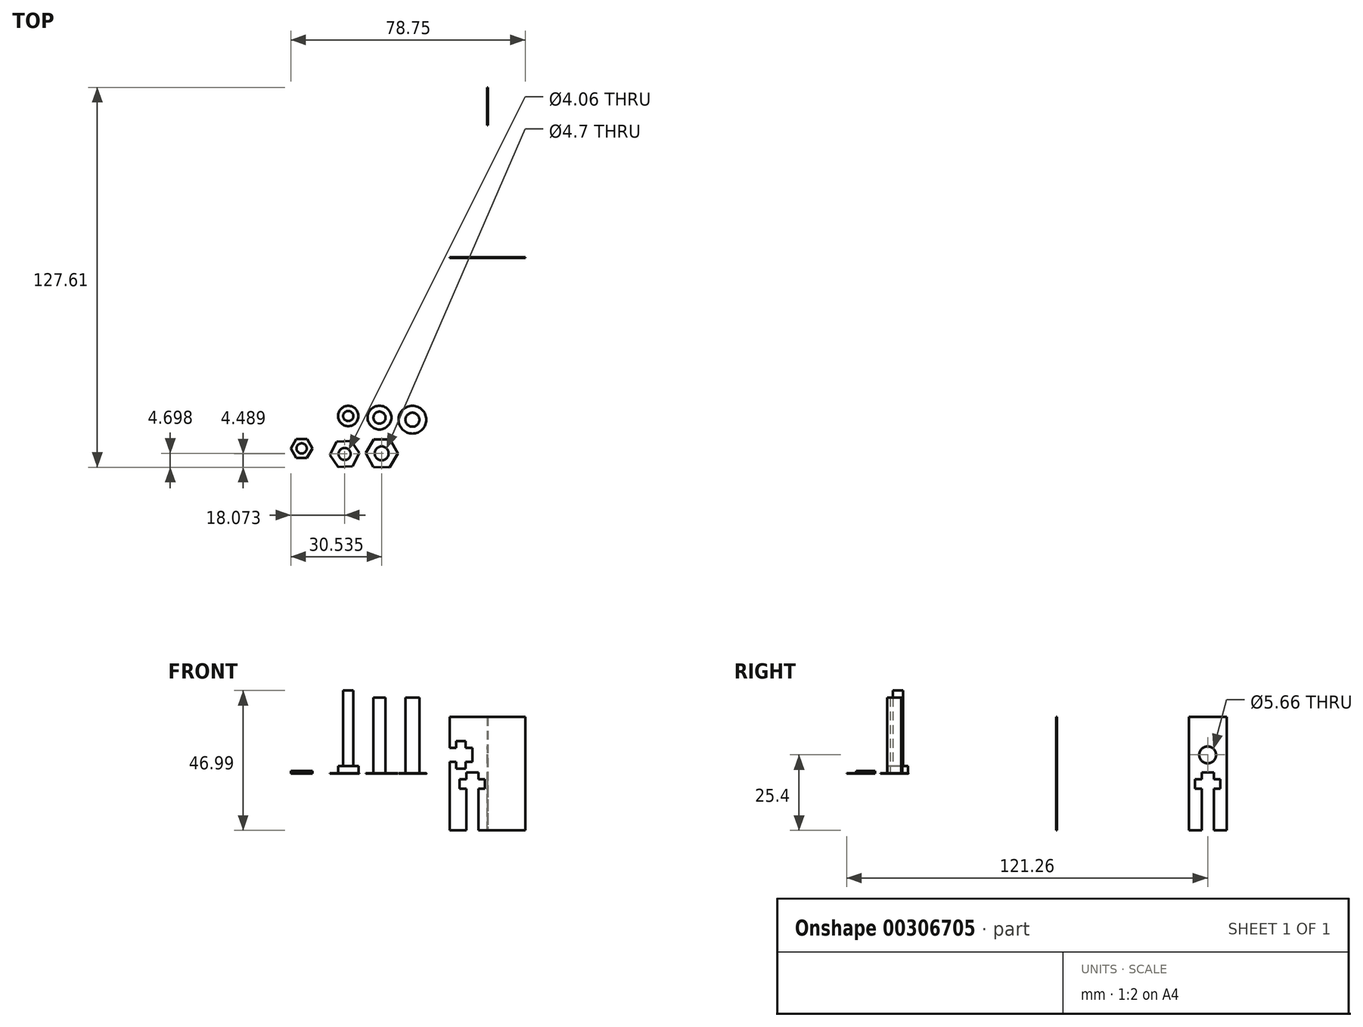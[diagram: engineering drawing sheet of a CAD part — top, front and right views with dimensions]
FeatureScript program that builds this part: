
annotation { "Feature Type Name" : "Feature", "Feature Type Description" : "" }
export const myFeature = defineFeature(function(context is Context, id is Id, definition is map)
    precondition{}
    {
        {
            assignVariable(context, id + "F0", {"name" : "mdfThick", "anyValue" : .235});
        }
        {
            var Q0;
            Q0=qCreatedBy(makeId("Front.planeOp"),FACE);
            var sketch = newSketch(context, id + "F1", { "sketchPlane" : qUnion([Q0])});
            skLineSegment(sketch, "E0.bottom", {"start": v(12.7, 19.05) * mm, "end": v(-12.7, 19.05) * mm});
            skLineSegment(sketch, "E0.top", {"start": v(12.7, -19.05) * mm, "end": v(-12.7, -19.05) * mm});
            skLineSegment(sketch, "E0.left", {"start": v(12.7, 19.05) * mm, "end": v(12.7, -19.05) * mm});
            skLineSegment(sketch, "E0.right", {"start": v(-12.7, 19.05) * mm, "end": v(-12.7, -19.05) * mm});
            skPoint(sketch, "E0.middle", {"position": v(0, 0) * mm});
            skSolve(sketch);
        }
        {
            var Q0;
            Q0 = qSketchRegion(id + "F1", true);
            extrude(context, id + "F2", {"entities" : qUnion([Q0]), "depth" : (getVariable(context, 'mdfThick')) * mm, "symmetric" : true});
        }
        {
            assignVariable(context, id + "F3", {"name" : "h1024", "anyValue" : .125});
        }
        {
            assignVariable(context, id + "F4", {"name" : "h632", "anyValue" : .95});
        }
        {
            assignVariable(context, id + "F5", {"name" : "h836", "anyValue" : .124});
        }
        {
            var Q0;
            Q0=makeQuery(id+"F2.opExtrude","CAP_FACE",FACE,{"disambiguationData":[OSD([sQuery(id+"F1.wireOp",EDGE,"E0.bottom"),sQuery(id+"F1.wireOp",EDGE,"E0.top"),sQuery(id+"F1.wireOp",EDGE,"E0.left"),sQuery(id+"F1.wireOp",EDGE,"E0.right")])],"isStart":false});
            var sketch = newSketch(context, id + "F6", { "sketchPlane" : qUnion([Q0])});
            skLineSegment(sketch, "E1", {"start": v(-12.7, -19.05) * mm, "end": v(-5.08, -19.05) * mm});
            skLineSegment(sketch, "E2", {"start": v(-12.7, -19.05) * mm, "end": v(-12.7, 6.35) * mm});
            skLineSegment(sketch, "E3.bottom", {"start": v(-5.08, 4) * mm, "end": v(-20.32, 4) * mm});
            skLineSegment(sketch, "E3.top", {"start": v(-5.08, 8.7) * mm, "end": v(-20.32, 8.7) * mm});
            skLineSegment(sketch, "E3.left", {"start": v(-5.08, 4) * mm, "end": v(-5.08, 8.7) * mm});
            skLineSegment(sketch, "E3.right", {"start": v(-20.32, 4) * mm, "end": v(-20.32, 8.7) * mm});
            skPoint(sketch, "E3.middle", {"position": v(-12.7, 6.35) * mm});
            skLineSegment(sketch, "E4.bottom", {"start": v(-3.05, 0.38) * mm, "end": v(-7.11, 0.38) * mm});
            skLineSegment(sketch, "E4.top", {"start": v(-3.05, -38.48) * mm, "end": v(-7.11, -38.48) * mm});
            skLineSegment(sketch, "E4.left", {"start": v(-3.05, 0.38) * mm, "end": v(-3.05, -38.48) * mm});
            skLineSegment(sketch, "E4.right", {"start": v(-7.11, 0.38) * mm, "end": v(-7.11, -38.48) * mm});
            skPoint(sketch, "E4.middle", {"position": v(-5.08, -19.05) * mm});
            skLineSegment(sketch, "E5", {"start": v(-5.08, 6.35) * mm, "end": v(-8.9, 6.35) * mm});
            skLineSegment(sketch, "E6.bottom", {"start": v(-7.3, 11.02) * mm, "end": v(-10.48, 11.02) * mm});
            skLineSegment(sketch, "E6.top", {"start": v(-7.3, 1.68) * mm, "end": v(-10.48, 1.68) * mm});
            skLineSegment(sketch, "E6.left", {"start": v(-7.3, 11.02) * mm, "end": v(-7.3, 1.68) * mm});
            skLineSegment(sketch, "E6.right", {"start": v(-10.48, 11.02) * mm, "end": v(-10.48, 1.68) * mm});
            skPoint(sketch, "E6.middle", {"position": v(-8.9, 6.35) * mm});
            skLineSegment(sketch, "E7", {"start": v(-5.08, 0.38) * mm, "end": v(-5.08, -3.43) * mm});
            skLineSegment(sketch, "E8.bottom", {"start": v(-0.83, -1.85) * mm, "end": v(-9.33, -1.85) * mm});
            skLineSegment(sketch, "E8.top", {"start": v(-0.83, -5) * mm, "end": v(-9.33, -5) * mm});
            skLineSegment(sketch, "E8.left", {"start": v(-0.83, -1.85) * mm, "end": v(-0.83, -5) * mm});
            skLineSegment(sketch, "E8.right", {"start": v(-9.33, -1.85) * mm, "end": v(-9.33, -5) * mm});
            skPoint(sketch, "E8.middle", {"position": v(-5.08, -3.43) * mm});
            skSolve(sketch);
        }
        {
            var Q0;
            {var subQ5=makeQuery(id+"F2.opExtrude","CAP_EDGE",EDGE,{"disambiguationData":[OSD([sQuery(id+"F1.wireOp",EDGE,"E0.right")])],"isStart":false});var subQ7=sQuery(id+"F6.wireOp",EDGE,"E2");var subQ9=makeQuery(id+"F6.imprint","INTERSECT",VERTEX,{"derivedFrom":[subQ5,subQ7]});Q0=makeQuery(id+"F6.imprint","IMPRINT",FACE,{"disambiguationData":[TD([[makeQuery(id+"F6.imprint","IMPRINT",EDGE,{"disambiguationData":[TD([[subQ9,-1.0]])],"derivedFrom":subQ7}),1.0]])]});}
            var Q1;
            {var subQ5=sQuery(id+"F6.wireOp",EDGE,"E6.bottom");Q1=makeQuery(id+"F6.imprint","IMPRINT",FACE,{"disambiguationData":[TD([[makeQuery(id+"F6.imprint","IMPRINT",EDGE,{"derivedFrom":subQ5}),1.0]])]});}
            var Q2;
            {var subQ0=sQuery(id+"F6.wireOp",EDGE,"E6.left");var subQ2=sQuery(id+"F6.wireOp",EDGE,"E3.bottom");var subQ3=makeQuery(id+"F6.imprint","INTERSECT",VERTEX,{"derivedFrom":[subQ2,subQ0]});Q2=makeQuery(id+"F6.imprint","IMPRINT",FACE,{"disambiguationData":[TD([[makeQuery(id+"F6.imprint","IMPRINT",EDGE,{"disambiguationData":[TD([[subQ3,-1.0]])],"derivedFrom":subQ2}),-1.0]])]});}
            var Q3;
            {var subQ0=sQuery(id+"F6.wireOp",EDGE,"E3.left");var subQ1=sQuery(id+"F6.wireOp",EDGE,"E3.top");var subQ2=makeQuery(id+"F6.imprint","INTERSECT",VERTEX,{"derivedFrom":[subQ1,subQ0]});Q3=makeQuery(id+"F6.imprint","IMPRINT",FACE,{"disambiguationData":[TD([[makeQuery(id+"F6.imprint","IMPRINT",EDGE,{"disambiguationData":[TD([[subQ2,-1.0]])],"derivedFrom":subQ1}),1.0]])]});}
            var Q4;
            {var subQ0=sQuery(id+"F6.wireOp",EDGE,"E3.left");var subQ1=sQuery(id+"F6.wireOp",EDGE,"E3.bottom");var subQ2=makeQuery(id+"F6.imprint","INTERSECT",VERTEX,{"derivedFrom":[subQ1,subQ0]});Q4=makeQuery(id+"F6.imprint","IMPRINT",FACE,{"disambiguationData":[TD([[makeQuery(id+"F6.imprint","IMPRINT",EDGE,{"disambiguationData":[TD([[subQ2,-1.0]])],"derivedFrom":subQ1}),-1.0]])]});}
            var Q5;
            {var subQ5=sQuery(id+"F6.wireOp",EDGE,"E6.top");Q5=makeQuery(id+"F6.imprint","IMPRINT",FACE,{"disambiguationData":[TD([[makeQuery(id+"F6.imprint","IMPRINT",EDGE,{"derivedFrom":subQ5}),-1.0]])]});}
            var Q6;
            {var subQ0=sQuery(id+"F6.wireOp",EDGE,"E4.left");var subQ1=sQuery(id+"F6.wireOp",EDGE,"E4.bottom");var subQ2=makeQuery(id+"F6.imprint","INTERSECT",VERTEX,{"derivedFrom":[subQ1,subQ0]});Q6=makeQuery(id+"F6.imprint","IMPRINT",FACE,{"disambiguationData":[TD([[makeQuery(id+"F6.imprint","IMPRINT",EDGE,{"disambiguationData":[TD([[subQ2,-1.0]])],"derivedFrom":subQ1}),1.0]])]});}
            var Q7;
            {var subQ0=sQuery(id+"F6.wireOp",EDGE,"E4.right");var subQ1=sQuery(id+"F6.wireOp",EDGE,"E4.bottom");var subQ2=makeQuery(id+"F6.imprint","INTERSECT",VERTEX,{"derivedFrom":[subQ1,subQ0]});Q7=makeQuery(id+"F6.imprint","IMPRINT",FACE,{"disambiguationData":[TD([[makeQuery(id+"F6.imprint","IMPRINT",EDGE,{"disambiguationData":[TD([[subQ2,1.0]])],"derivedFrom":subQ1}),1.0]])]});}
            var Q8;
            {var subQ0=sQuery(id+"F6.wireOp",EDGE,"E8.bottom");var subQ2=sQuery(id+"F6.wireOp",EDGE,"E4.left");var subQ3=makeQuery(id+"F6.imprint","INTERSECT",VERTEX,{"derivedFrom":[subQ2,subQ0]});Q8=makeQuery(id+"F6.imprint","IMPRINT",FACE,{"disambiguationData":[TD([[makeQuery(id+"F6.imprint","IMPRINT",EDGE,{"disambiguationData":[TD([[subQ3,-1.0]])],"derivedFrom":subQ2}),-1.0]])]});}
            var Q9;
            {var subQ5=sQuery(id+"F6.wireOp",EDGE,"E8.right");Q9=makeQuery(id+"F6.imprint","IMPRINT",FACE,{"disambiguationData":[TD([[makeQuery(id+"F6.imprint","IMPRINT",EDGE,{"derivedFrom":subQ5}),1.0]])]});}
            var Q10;
            {var subQ5=sQuery(id+"F6.wireOp",EDGE,"E8.left");Q10=makeQuery(id+"F6.imprint","IMPRINT",FACE,{"disambiguationData":[TD([[makeQuery(id+"F6.imprint","IMPRINT",EDGE,{"derivedFrom":subQ5}),-1.0]])]});}
            var Q11;
            {var subQ5=makeQuery(id+"F2.opExtrude","CAP_EDGE",EDGE,{"disambiguationData":[OSD([sQuery(id+"F1.wireOp",EDGE,"E0.top")])],"isStart":false});var subQ7=sQuery(id+"F6.wireOp",EDGE,"E1");var subQ9=makeQuery(id+"F6.imprint","INTERSECT",VERTEX,{"derivedFrom":[subQ5,subQ7]});Q11=makeQuery(id+"F6.imprint","IMPRINT",FACE,{"disambiguationData":[TD([[makeQuery(id+"F6.imprint","IMPRINT",EDGE,{"disambiguationData":[TD([[subQ9,-1.0]])],"derivedFrom":subQ7}),-1.0]])]});}
            extrude(context, id + "F7", {"entities" : qUnion([Q0, Q1, Q2, Q3, Q4, Q5, Q6, Q7, Q8, Q9, Q10, Q11]), "operationType" : NewBodyOperationType.REMOVE, "endBound" : BoundingType.UP_TO_NEXT, "oppositeDirection" : true, "depth" : 25.4 * mm});
        }
        {
            var Q0;
            Q0=qCreatedBy(makeId("Top.planeOp"),FACE);
            var sketch = newSketch(context, id + "F8", { "sketchPlane" : qUnion([Q0])});
            skCircle(sketch, "E9", {"center": v(-46.73, -53.22) * mm, "radius": 3.4 * mm});
            skSolve(sketch);
        }
        {
            var Q0;
            Q0=makeQuery(id+"F8.imprint","IMPRINT",FACE,{"disambiguationData":[TD([[makeQuery(id+"F8.imprint","IMPRINT",EDGE,{"derivedFrom":sQuery(id+"F8.wireOp",EDGE,"E9")}),1.0]])]});
            extrude(context, id + "F9", {"entities" : qUnion([Q0]), "depth" : 2.54 * mm});
        }
        {
            var Q0;
            Q0=makeQuery(id+"F9.opExtrude","CAP_FACE",FACE,{"disambiguationData":[OSD([sQuery(id+"F8.wireOp",EDGE,"E9")])],"isStart":false});
            var sketch = newSketch(context, id + "F10", { "sketchPlane" : qUnion([Q0])});
            skCircle(sketch, "E10", {"center": v(-46.73, -53.22) * mm, "radius": 1.71 * mm});
            skSolve(sketch);
        }
        {
            var Q0;
            Q0=makeQuery(id+"F10.imprint","IMPRINT",FACE,{"disambiguationData":[TD([[makeQuery(id+"F10.imprint","IMPRINT",EDGE,{"derivedFrom":sQuery(id+"F10.wireOp",EDGE,"E10")}),1.0]])]});
            extrude(context, id + "F11", {"entities" : qUnion([Q0]), "operationType" : NewBodyOperationType.ADD, "depth" : 25.4 * mm});
        }
        {
            var Q0;
            Q0=qCreatedBy(makeId("Top.planeOp"),FACE);
            var sketch = newSketch(context, id + "F12", { "sketchPlane" : qUnion([Q0])});
            skCircle(sketch, "E11.cCircle", {"center": v(-62.4, -64.12) * mm, "radius": 3.15 * mm, "construction": true});
            skLineSegment(sketch, "E11.0", {"start": v(-60.58, -60.98) * mm, "end": v(-58.77, -64.14) * mm});
            skLineSegment(sketch, "E11.1", {"start": v(-58.77, -64.14) * mm, "end": v(-60.6, -67.28) * mm});
            skLineSegment(sketch, "E11.2", {"start": v(-60.6, -67.28) * mm, "end": v(-64.24, -67.26) * mm});
            skLineSegment(sketch, "E11.3", {"start": v(-64.24, -67.26) * mm, "end": v(-66.05, -64.1) * mm});
            skLineSegment(sketch, "E11.4", {"start": v(-66.05, -64.1) * mm, "end": v(-64.21, -60.96) * mm});
            skLineSegment(sketch, "E11.5", {"start": v(-64.21, -60.96) * mm, "end": v(-60.58, -60.98) * mm});
            skPoint(sketch, "E11.0.midPoint", {"position": v(-59.67, -62.56) * mm});
            skCircle(sketch, "E12", {"center": v(-62.4, -64.12) * mm, "radius": 1.71 * mm});
            skCircle(sketch, "E13.cCircle", {"center": v(-47.98, -65.97) * mm, "radius": 4.25 * mm, "construction": true});
            skLineSegment(sketch, "E13.0", {"start": v(-43.07, -65.66) * mm, "end": v(-45.26, -70.06) * mm});
            skLineSegment(sketch, "E13.1", {"start": v(-45.26, -70.06) * mm, "end": v(-50.16, -70.37) * mm});
            skLineSegment(sketch, "E13.2", {"start": v(-50.16, -70.37) * mm, "end": v(-52.88, -66.28) * mm});
            skLineSegment(sketch, "E13.3", {"start": v(-52.88, -66.28) * mm, "end": v(-50.7, -61.88) * mm});
            skLineSegment(sketch, "E13.4", {"start": v(-50.7, -61.88) * mm, "end": v(-45.8, -61.57) * mm});
            skLineSegment(sketch, "E13.5", {"start": v(-45.8, -61.57) * mm, "end": v(-43.07, -65.66) * mm});
            skPoint(sketch, "E13.0.midPoint", {"position": v(-44.17, -67.86) * mm});
            skCircle(sketch, "E14.cCircle", {"center": v(-35.52, -65.76) * mm, "radius": 4.67 * mm, "construction": true});
            skLineSegment(sketch, "E14.0", {"start": v(-30.12, -65.82) * mm, "end": v(-32.86, -70.46) * mm});
            skLineSegment(sketch, "E14.1", {"start": v(-32.86, -70.46) * mm, "end": v(-38.26, -70.4) * mm});
            skLineSegment(sketch, "E14.2", {"start": v(-38.26, -70.4) * mm, "end": v(-40.91, -65.7) * mm});
            skLineSegment(sketch, "E14.3", {"start": v(-40.91, -65.7) * mm, "end": v(-38.17, -61.06) * mm});
            skLineSegment(sketch, "E14.4", {"start": v(-38.17, -61.06) * mm, "end": v(-32.77, -61.12) * mm});
            skLineSegment(sketch, "E14.5", {"start": v(-32.77, -61.12) * mm, "end": v(-30.12, -65.82) * mm});
            skPoint(sketch, "E14.0.midPoint", {"position": v(-31.5, -68.14) * mm});
            skCircle(sketch, "E15", {"center": v(-47.98, -65.97) * mm, "radius": 2.03 * mm});
            skCircle(sketch, "E16", {"center": v(-35.52, -65.76) * mm, "radius": 2.35 * mm});
            skSolve(sketch);
        }
        {
            var Q0;
            Q0=makeQuery(id+"F12.imprint","IMPRINT",FACE,{"disambiguationData":[TD([[makeQuery(id+"F12.imprint","IMPRINT",EDGE,{"derivedFrom":sQuery(id+"F12.wireOp",EDGE,"E11.0")}),-1.0]])]});
            extrude(context, id + "F13", {"entities" : qUnion([Q0]), "depth" : (getVariable(context, 'h632')) * mm});
        }
        {
            var Q0;
            Q0=makeQuery(id+"F12.imprint","IMPRINT",FACE,{"disambiguationData":[TD([[makeQuery(id+"F12.imprint","IMPRINT",EDGE,{"derivedFrom":sQuery(id+"F12.wireOp",EDGE,"E13.0")}),-1.0]])]});
            extrude(context, id + "F14", {"entities" : qUnion([Q0]), "depth" : (getVariable(context, 'h836')) * mm});
        }
        {
            var Q0;
            Q0=makeQuery(id+"F12.imprint","IMPRINT",FACE,{"disambiguationData":[TD([[makeQuery(id+"F12.imprint","IMPRINT",EDGE,{"derivedFrom":sQuery(id+"F12.wireOp",EDGE,"E14.0")}),-1.0]])]});
            extrude(context, id + "F15", {"entities" : qUnion([Q0]), "depth" : (getVariable(context, 'h1024')) * mm});
        }
        {
            var Q0;
            Q0=qCreatedBy(makeId("Top.planeOp"),FACE);
            var sketch = newSketch(context, id + "F16", { "sketchPlane" : qUnion([Q0])});
            skCircle(sketch, "E17", {"center": v(-36.25, -53.75) * mm, "radius": 3.99 * mm});
            skCircle(sketch, "E18", {"center": v(-25.2, -54.47) * mm, "radius": 4.66 * mm});
            skSolve(sketch);
        }
        {
            var Q0;
            Q0=makeQuery(id+"F16.imprint","IMPRINT",FACE,{"disambiguationData":[TD([[makeQuery(id+"F16.imprint","IMPRINT",EDGE,{"derivedFrom":sQuery(id+"F16.wireOp",EDGE,"E17")}),1.0]])]});
            extrude(context, id + "F17", {"entities" : qUnion([Q0]), "depth" : (getVariable(context, 'h836')) * mm});
        }
        {
            var Q0;
            Q0=makeQuery(id+"F16.imprint","IMPRINT",FACE,{"disambiguationData":[TD([[makeQuery(id+"F16.imprint","IMPRINT",EDGE,{"derivedFrom":sQuery(id+"F16.wireOp",EDGE,"E18")}),1.0]])]});
            extrude(context, id + "F18", {"entities" : qUnion([Q0]), "depth" : (getVariable(context, 'h1024')) * mm});
        }
        {
            var Q0;
            Q0=makeQuery(id+"F17.opExtrude","CAP_FACE",FACE,{"disambiguationData":[OSD([sQuery(id+"F16.wireOp",EDGE,"E17")])],"isStart":false});
            var sketch = newSketch(context, id + "F19", { "sketchPlane" : qUnion([Q0])});
            skCircle(sketch, "E19", {"center": v(-36.25, -53.75) * mm, "radius": 2.03 * mm});
            skSolve(sketch);
        }
        {
            var Q0;
            Q0=makeQuery(id+"F18.opExtrude","CAP_FACE",FACE,{"disambiguationData":[OSD([sQuery(id+"F16.wireOp",EDGE,"E18")])],"isStart":false});
            var sketch = newSketch(context, id + "F20", { "sketchPlane" : qUnion([Q0])});
            skCircle(sketch, "E20", {"center": v(-25.2, -54.47) * mm, "radius": 2.35 * mm});
            skSolve(sketch);
        }
        {
            var Q0;
            Q0=makeQuery(id+"F19.imprint","IMPRINT",FACE,{"disambiguationData":[TD([[makeQuery(id+"F19.imprint","IMPRINT",EDGE,{"derivedFrom":sQuery(id+"F19.wireOp",EDGE,"E19")}),1.0]])]});
            extrude(context, id + "F21", {"entities" : qUnion([Q0]), "operationType" : NewBodyOperationType.ADD, "depth" : 25.4 * mm});
        }
        {
            var Q0;
            Q0=makeQuery(id+"F20.imprint","IMPRINT",FACE,{"disambiguationData":[TD([[makeQuery(id+"F20.imprint","IMPRINT",EDGE,{"derivedFrom":sQuery(id+"F20.wireOp",EDGE,"E20")}),1.0]])]});
            extrude(context, id + "F22", {"entities" : qUnion([Q0]), "operationType" : NewBodyOperationType.ADD, "depth" : 25.4 * mm});
        }
        {
            var Q0;
            Q0=qCreatedBy(makeId("Right.planeOp"),FACE);
            var sketch = newSketch(context, id + "F23", { "sketchPlane" : qUnion([Q0])});
            skLineSegment(sketch, "E21", {"start": v(0, 0) * mm, "end": v(50.8, 0) * mm});
            skLineSegment(sketch, "E22.bottom", {"start": v(57.15, 19.05) * mm, "end": v(44.45, 19.05) * mm});
            skLineSegment(sketch, "E22.top", {"start": v(57.15, -19.05) * mm, "end": v(44.45, -19.05) * mm});
            skLineSegment(sketch, "E22.left", {"start": v(57.15, 19.05) * mm, "end": v(57.15, -19.05) * mm});
            skLineSegment(sketch, "E22.right", {"start": v(44.45, 19.05) * mm, "end": v(44.45, -19.05) * mm});
            skPoint(sketch, "E22.middle", {"position": v(50.8, 0) * mm});
            skSolve(sketch);
        }
        {
            var Q0;
            {var subQ0=sQuery(id+"F23.wireOp",EDGE,"E22.bottom");Q0=makeQuery(id+"F23.imprint","IMPRINT",FACE,{"disambiguationData":[TD([[makeQuery(id+"F23.imprint","IMPRINT",EDGE,{"derivedFrom":subQ0}),1.0]])]});}
            extrude(context, id + "F24", {"entities" : qUnion([Q0]), "depth" : (getVariable(context, 'mdfThick')) * mm, "symmetric" : true});
        }
        {
            var Q0;
            Q0=makeQuery(id+"F24.opExtrude","CAP_FACE",FACE,{"disambiguationData":[OSD([sQuery(id+"F23.wireOp",EDGE,"E22.bottom"),sQuery(id+"F23.wireOp",EDGE,"E22.top"),sQuery(id+"F23.wireOp",EDGE,"E22.left"),sQuery(id+"F23.wireOp",EDGE,"E22.right")])],"isStart":false});
            var sketch = newSketch(context, id + "F25", { "sketchPlane" : qUnion([Q0])});
            skLineSegment(sketch, "E23.bottom", {"start": v(52.83, 0.38) * mm, "end": v(48.77, 0.38) * mm});
            skLineSegment(sketch, "E23.top", {"start": v(52.83, -38.48) * mm, "end": v(48.77, -38.48) * mm});
            skLineSegment(sketch, "E23.left", {"start": v(52.83, 0.38) * mm, "end": v(52.83, -38.48) * mm});
            skLineSegment(sketch, "E23.right", {"start": v(48.77, 0.38) * mm, "end": v(48.77, -38.48) * mm});
            skPoint(sketch, "E23.middle", {"position": v(50.8, -19.05) * mm});
            skLineSegment(sketch, "E24", {"start": v(50.8, 0.38) * mm, "end": v(50.8, -3.43) * mm});
            skLineSegment(sketch, "E25.bottom", {"start": v(55.05, -5) * mm, "end": v(46.55, -5) * mm});
            skLineSegment(sketch, "E25.top", {"start": v(55.05, -1.85) * mm, "end": v(46.55, -1.85) * mm});
            skLineSegment(sketch, "E25.left", {"start": v(55.05, -5) * mm, "end": v(55.05, -1.85) * mm});
            skLineSegment(sketch, "E25.right", {"start": v(46.55, -5) * mm, "end": v(46.55, -1.85) * mm});
            skPoint(sketch, "E25.middle", {"position": v(50.8, -3.43) * mm});
            skLineSegment(sketch, "E26", {"start": v(50.8, 0.38) * mm, "end": v(50.8, 6.35) * mm});
            skCircle(sketch, "E27", {"center": v(50.8, 6.35) * mm, "radius": 2.83 * mm});
            skSolve(sketch);
        }
        {
            var Q0;
            Q0=makeQuery(id+"F25.imprint","IMPRINT",FACE,{"disambiguationData":[TD([[makeQuery(id+"F25.imprint","IMPRINT",EDGE,{"derivedFrom":sQuery(id+"F25.wireOp",EDGE,"E27")}),1.0]])]});
            var Q1;
            {var subQ0=sQuery(id+"F25.wireOp",EDGE,"E23.left");var subQ1=sQuery(id+"F25.wireOp",EDGE,"E23.bottom");var subQ2=makeQuery(id+"F25.imprint","INTERSECT",VERTEX,{"derivedFrom":[subQ1,subQ0]});Q1=makeQuery(id+"F25.imprint","IMPRINT",FACE,{"disambiguationData":[TD([[makeQuery(id+"F25.imprint","IMPRINT",EDGE,{"disambiguationData":[TD([[subQ2,-1.0]])],"derivedFrom":subQ1}),1.0]])]});}
            var Q2;
            {var subQ0=sQuery(id+"F25.wireOp",EDGE,"E23.right");var subQ1=sQuery(id+"F25.wireOp",EDGE,"E23.bottom");var subQ2=makeQuery(id+"F25.imprint","INTERSECT",VERTEX,{"derivedFrom":[subQ1,subQ0]});Q2=makeQuery(id+"F25.imprint","IMPRINT",FACE,{"disambiguationData":[TD([[makeQuery(id+"F25.imprint","IMPRINT",EDGE,{"disambiguationData":[TD([[subQ2,1.0]])],"derivedFrom":subQ1}),1.0]])]});}
            var Q3;
            {var subQ0=sQuery(id+"F25.wireOp",EDGE,"E25.top");var subQ2=sQuery(id+"F25.wireOp",EDGE,"E23.left");var subQ3=makeQuery(id+"F25.imprint","INTERSECT",VERTEX,{"derivedFrom":[subQ2,subQ0]});Q3=makeQuery(id+"F25.imprint","IMPRINT",FACE,{"disambiguationData":[TD([[makeQuery(id+"F25.imprint","IMPRINT",EDGE,{"disambiguationData":[TD([[subQ3,-1.0]])],"derivedFrom":subQ2}),-1.0]])]});}
            var Q4;
            {var subQ5=sQuery(id+"F25.wireOp",EDGE,"E25.right");Q4=makeQuery(id+"F25.imprint","IMPRINT",FACE,{"disambiguationData":[TD([[makeQuery(id+"F25.imprint","IMPRINT",EDGE,{"derivedFrom":subQ5}),-1.0]])]});}
            var Q5;
            {var subQ5=sQuery(id+"F25.wireOp",EDGE,"E25.left");Q5=makeQuery(id+"F25.imprint","IMPRINT",FACE,{"disambiguationData":[TD([[makeQuery(id+"F25.imprint","IMPRINT",EDGE,{"derivedFrom":subQ5}),1.0]])]});}
            var Q6;
            {var subQ0=sQuery(id+"F25.wireOp",EDGE,"E25.bottom");var subQ1=sQuery(id+"F25.wireOp",EDGE,"E23.left");var subQ2=makeQuery(id+"F25.imprint","INTERSECT",VERTEX,{"derivedFrom":[subQ1,subQ0]});Q6=makeQuery(id+"F25.imprint","IMPRINT",FACE,{"disambiguationData":[TD([[makeQuery(id+"F25.imprint","IMPRINT",EDGE,{"disambiguationData":[TD([[subQ2,-1.0]])],"derivedFrom":subQ1}),-1.0]])]});}
            extrude(context, id + "F26", {"entities" : qUnion([Q0, Q1, Q2, Q3, Q4, Q5, Q6]), "operationType" : NewBodyOperationType.REMOVE, "endBound" : BoundingType.UP_TO_NEXT, "oppositeDirection" : true, "depth" : 25.4 * mm});
        }
    });
